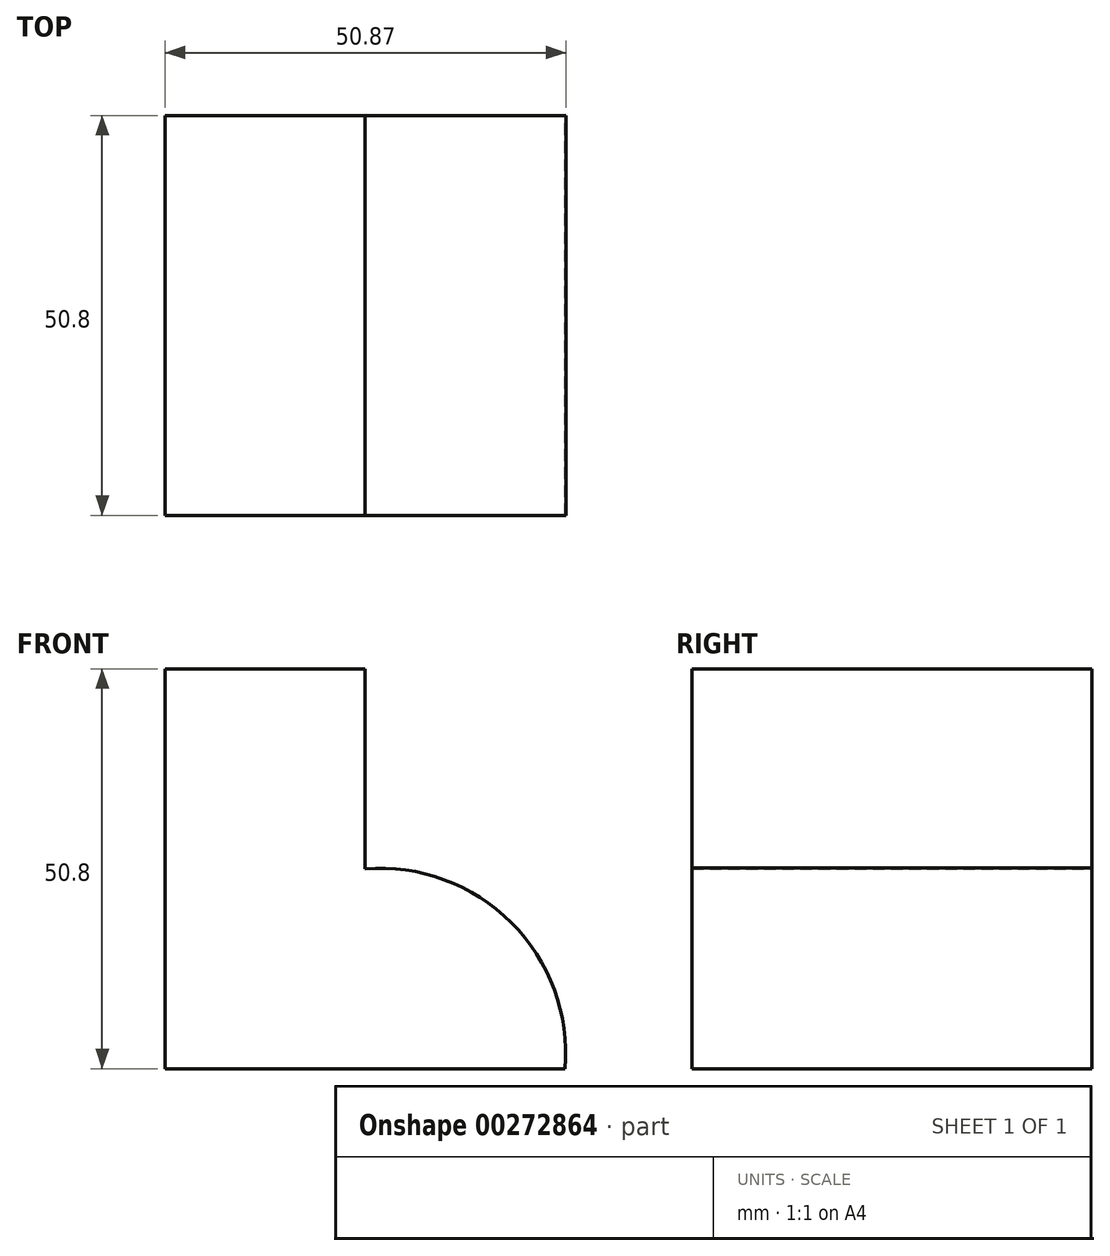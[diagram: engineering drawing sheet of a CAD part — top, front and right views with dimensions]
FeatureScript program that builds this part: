
annotation { "Feature Type Name" : "Feature", "Feature Type Description" : "" }
export const myFeature = defineFeature(function(context is Context, id is Id, definition is map)
    precondition{}
    {
        {
            var Q0;
            Q0=qCreatedBy(makeId("Front.planeOp"),FACE);
            var sketch = newSketch(context, id + "F0", { "sketchPlane" : qUnion([Q0])});
            skLineSegment(sketch, "E0", {"start": v(0, 0) * mm, "end": v(0, 50.8) * mm});
            skLineSegment(sketch, "E1", {"start": v(0, 0) * mm, "end": v(50.8, 0) * mm});
            skLineSegment(sketch, "E2", {"start": v(0, 50.8) * mm, "end": v(25.4, 50.8) * mm});
            skLineSegment(sketch, "E3", {"start": v(25.4, 50.8) * mm, "end": v(25.4, 25.4) * mm});
            skArc(sketch, "E4", {"start": v(50.8, 0) * mm, "mid": v(43.95, 18.55) * mm, "end": v(25.4, 25.4) * mm});
            skSolve(sketch);
        }
        {
            var Q0;
            Q0 = qSketchRegion(id + "F0", true);
            extrude(context, id + "F1", {"entities" : qUnion([Q0]), "depth" : 50.8 * mm});
        }
    });
